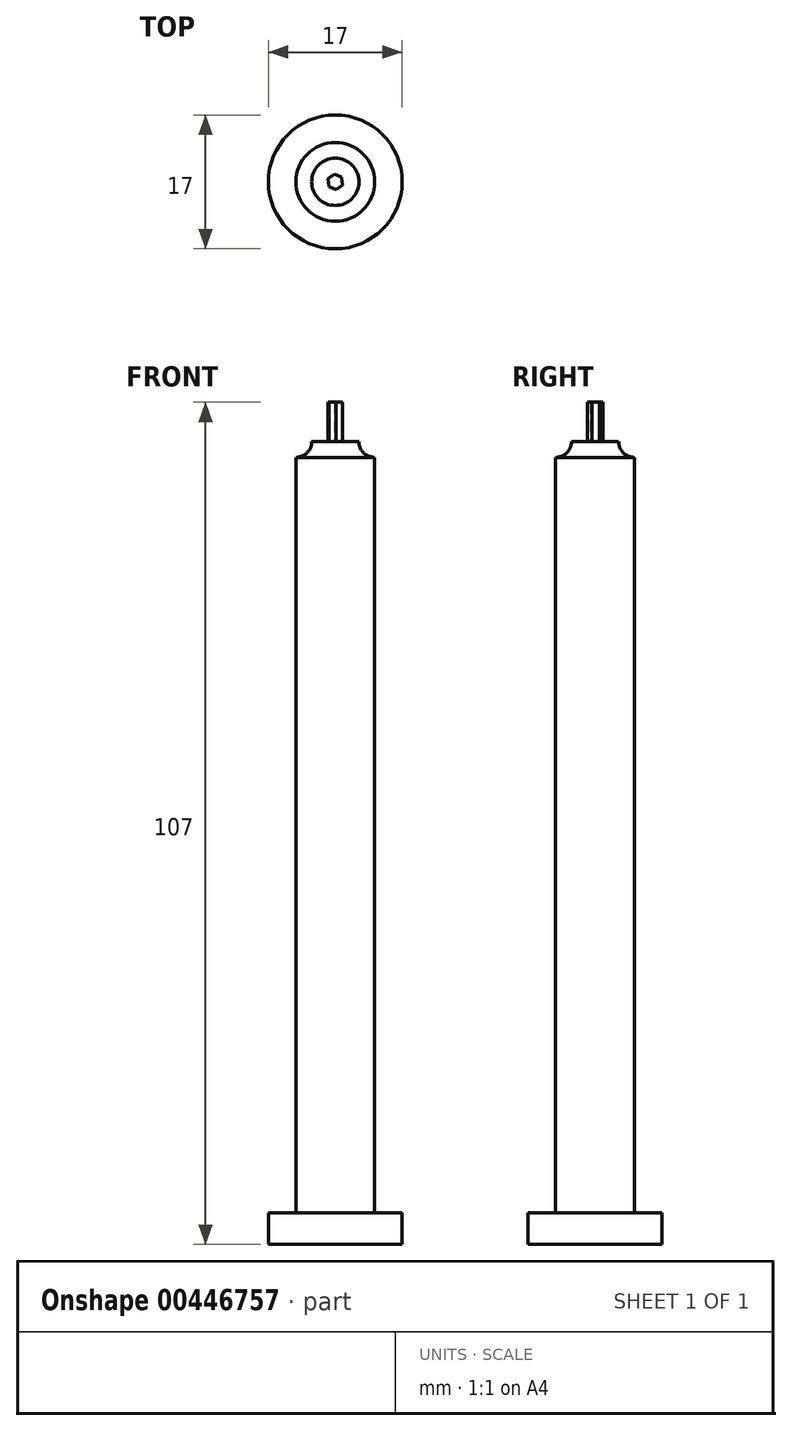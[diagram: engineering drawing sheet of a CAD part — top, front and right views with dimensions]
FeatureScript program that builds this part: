
annotation { "Feature Type Name" : "Feature", "Feature Type Description" : "" }
export const myFeature = defineFeature(function(context is Context, id is Id, definition is map)
    precondition{}
    {
        {
            var Q0;
            Q0=qCreatedBy(makeId("Top.planeOp"),FACE);
            var sketch = newSketch(context, id + "F0", { "sketchPlane" : qUnion([Q0])});
            skCircle(sketch, "E0", {"center": v(0, 0) * mm, "radius": 8.5 * mm});
            skSolve(sketch);
        }
        {
            var Q0;
            Q0=qSketchRegion(id+"F0",true);
            extrude(context, id + "F1", {"entities" : qUnion([Q0]), "depth" : 4 * mm});
        }
        {
            var Q0;
            Q0=qCreatedBy(makeId("Top.planeOp"),FACE);
            var sketch = newSketch(context, id + "F2", { "sketchPlane" : qUnion([Q0])});
            skCircle(sketch, "E1", {"center": v(0, 0) * mm, "radius": 5 * mm});
            skSolve(sketch);
        }
        {
            var Q0;
            Q0=qSketchRegion(id+"F2",true);
            extrude(context, id + "F3", {"entities" : qUnion([Q0]), "operationType" : NewBodyOperationType.ADD, "depth" : 100 * mm});
        }
        {
            var Q0;
            Q0=qCreatedBy(makeId("Right.planeOp"),FACE);
            var sketch = newSketch(context, id + "F4", { "sketchPlane" : qUnion([Q0])});
            skLineSegment(sketch, "E2", {"start": v(0, 102) * mm, "end": v(0, 100) * mm});
            skLineSegment(sketch, "E3", {"start": v(0, 100) * mm, "end": v(5, 100) * mm});
            skLineSegment(sketch, "E4", {"start": v(3, 102) * mm, "end": v(0, 102) * mm});
            skArc(sketch, "E5", {"start": v(3, 102) * mm, "mid": v(3.59, 100.59) * mm, "end": v(5, 100) * mm});
            skSolve(sketch);
        }
        {
            var Q0;
            Q0=makeQuery(id+"F4.imprint","IMPRINT",FACE,{"disambiguationData":[TD([[makeQuery(id+"F4.imprint","IMPRINT",EDGE,{"derivedFrom":sQuery(id+"F4.wireOp",EDGE,"E2")}),1.0]])]});
            var Q1;
            Q1=sQuery(id+"F4.wireOp",EDGE,"E2");
            revolve(context, id + "F5", {"operationType" : NewBodyOperationType.ADD, "entities" : qUnion([Q0]), "axis" : qUnion([Q1]), "revolveType" : RevolveType.FULL});
        }
        {
            var Q0;
            Q0=makeQuery(id+"F5.opRevolve","SWEPT_FACE",FACE,{"disambiguationData":[OSD([sQuery(id+"F4.wireOp",EDGE,"E4")])]});
            var sketch = newSketch(context, id + "F6", { "sketchPlane" : qUnion([Q0])});
            skCircle(sketch, "E6.cCircle", {"center": v(0, 0) * mm, "radius": 0.87 * mm, "construction": true});
            skLineSegment(sketch, "E6.0", {"start": v(0.9, -0.42) * mm, "end": v(0.09, -1) * mm});
            skLineSegment(sketch, "E6.1", {"start": v(0.09, -1) * mm, "end": v(-0.82, -0.57) * mm});
            skLineSegment(sketch, "E6.2", {"start": v(-0.82, -0.57) * mm, "end": v(-0.9, 0.42) * mm});
            skLineSegment(sketch, "E6.3", {"start": v(-0.9, 0.42) * mm, "end": v(-0.09, 1) * mm});
            skLineSegment(sketch, "E6.4", {"start": v(-0.09, 1) * mm, "end": v(0.82, 0.57) * mm});
            skLineSegment(sketch, "E6.5", {"start": v(0.82, 0.57) * mm, "end": v(0.9, -0.42) * mm});
            skPoint(sketch, "E6.0.midPoint", {"position": v(0.5, -0.7) * mm});
            skSolve(sketch);
        }
        {
            var Q0;
            Q0=makeQuery(id+"F6.imprint","IMPRINT",FACE,{"disambiguationData":[TD([[makeQuery(id+"F6.imprint","IMPRINT",EDGE,{"derivedFrom":sQuery(id+"F6.wireOp",EDGE,"E6.0")}),-1.0]])]});
            extrude(context, id + "F7", {"entities" : qUnion([Q0]), "operationType" : NewBodyOperationType.ADD, "depth" : 5 * mm});
        }
    });
